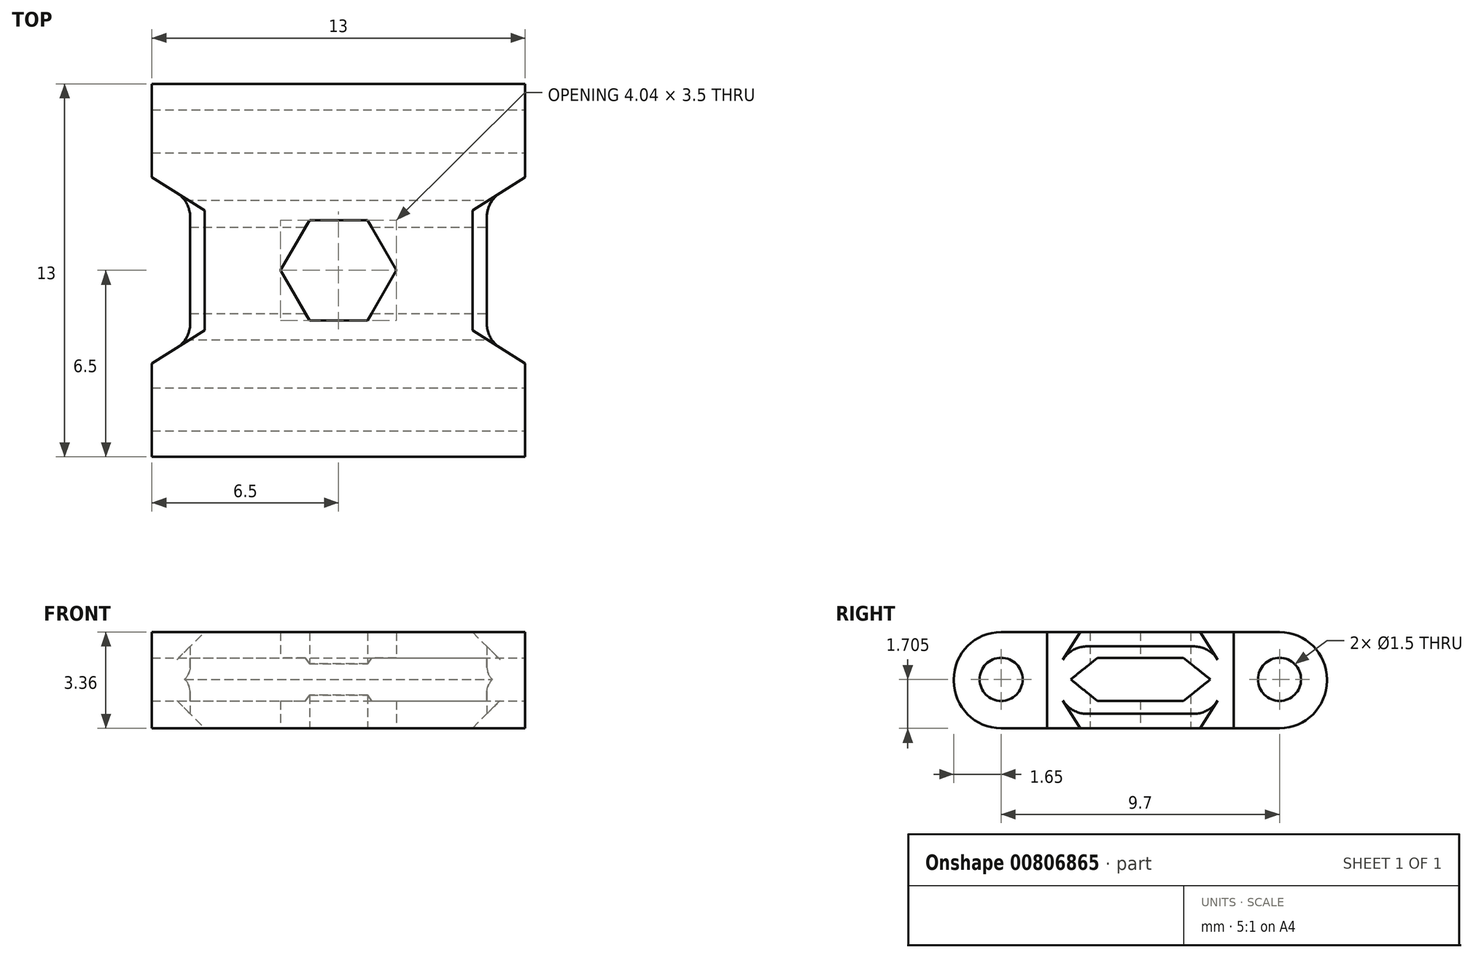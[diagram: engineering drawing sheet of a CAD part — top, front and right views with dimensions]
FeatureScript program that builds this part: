
annotation { "Feature Type Name" : "Feature", "Feature Type Description" : "" }
export const myFeature = defineFeature(function(context is Context, id is Id, definition is map)
    precondition{}
    {
        {
            var Q0;
            Q0=qCreatedBy(makeId("Top.planeOp"),FACE);
            var sketch = newSketch(context, id + "F0", { "sketchPlane" : qUnion([Q0])});
            skLineSegment(sketch, "E0.bottom", {"start": v(-6.5, 6.5) * mm, "end": v(6.5, 6.5) * mm});
            skLineSegment(sketch, "E0.top", {"start": v(-6.5, -6.5) * mm, "end": v(6.5, -6.5) * mm});
            skLineSegment(sketch, "E0.left", {"start": v(-6.5, 6.5) * mm, "end": v(-6.5, -6.5) * mm});
            skLineSegment(sketch, "E0.right", {"start": v(6.5, 6.5) * mm, "end": v(6.5, -6.5) * mm});
            skPoint(sketch, "E0.middle", {"position": v(0, 0) * mm});
            skLineSegment(sketch, "E1.bottom", {"start": v(-6.5, 3.25) * mm, "end": v(6.5, 3.25) * mm, "construction": true});
            skLineSegment(sketch, "E1.top", {"start": v(-6.5, -3.25) * mm, "end": v(6.5, -3.25) * mm, "construction": true});
            skLineSegment(sketch, "E1.left", {"start": v(-6.5, 3.25) * mm, "end": v(-6.5, -3.25) * mm, "construction": true});
            skLineSegment(sketch, "E1.right", {"start": v(6.5, 3.25) * mm, "end": v(6.5, -3.25) * mm, "construction": true});
            skLineSegment(sketch, "E2", {"start": v(-6.5, 3.25) * mm, "end": v(-5.17, 2.4) * mm});
            skLineSegment(sketch, "E3", {"start": v(-5.17, 2.4) * mm, "end": v(-5.17, -2.4) * mm});
            skLineSegment(sketch, "E4", {"start": v(-5.17, -2.4) * mm, "end": v(-6.5, -3.25) * mm});
            skLineSegment(sketch, "E5.MirrorCS", {"start": v(5.17, -2.4) * mm, "end": v(6.5, -3.25) * mm});
            skLineSegment(sketch, "E6.MirrorCS", {"start": v(6.5, 3.25) * mm, "end": v(5.17, 2.4) * mm});
            skLineSegment(sketch, "E7.MirrorCS", {"start": v(5.17, 2.4) * mm, "end": v(5.17, -2.4) * mm});
            skCircle(sketch, "E8.cCircle", {"center": v(0, 0) * mm, "radius": 1.75 * mm, "construction": true});
            skLineSegment(sketch, "E8.0", {"start": v(-1.01, 1.75) * mm, "end": v(1.01, 1.75) * mm});
            skLineSegment(sketch, "E8.1", {"start": v(1.01, 1.75) * mm, "end": v(2.02, 0) * mm});
            skLineSegment(sketch, "E8.2", {"start": v(2.02, 0) * mm, "end": v(1.01, -1.75) * mm});
            skLineSegment(sketch, "E8.3", {"start": v(1.01, -1.75) * mm, "end": v(-1.01, -1.75) * mm});
            skLineSegment(sketch, "E8.4", {"start": v(-1.01, -1.75) * mm, "end": v(-2.02, 0) * mm});
            skLineSegment(sketch, "E8.5", {"start": v(-2.02, 0) * mm, "end": v(-1.01, 1.75) * mm});
            skPoint(sketch, "E8.0.midPoint", {"position": v(0, 1.75) * mm});
            skSolve(sketch);
        }
        {
            var Q0;
            Q0=makeQuery(id+"F0.imprint","IMPRINT",FACE,{"disambiguationData":[TD([[makeQuery(id+"F0.imprint","IMPRINT",EDGE,{"derivedFrom":sQuery(id+"F0.wireOp",EDGE,"E0.bottom")}),-1.0]])]});
            extrude(context, id + "F1", {"entities" : qUnion([Q0]), "endBound" : BoundingType.SYMMETRIC, "depth" : 3.35 * mm, "offsetDistance" : 25.4 * mm});
        }
        {
            var Q0;
            Q0=makeQuery(id+"F1.opExtrude","CAP_EDGE",EDGE,{"disambiguationData":[OSD([sQuery(id+"F0.wireOp",EDGE,"E3")])],"isStart":false});
            var Q1;
            Q1=makeQuery(id+"F1.opExtrude","CAP_EDGE",EDGE,{"disambiguationData":[OSD([sQuery(id+"F0.wireOp",EDGE,"E7.MirrorCS")])],"isStart":false});
            var Q2;
            Q2=makeQuery(id+"F1.opExtrude","CAP_EDGE",EDGE,{"disambiguationData":[OSD([sQuery(id+"F0.wireOp",EDGE,"E3")])],"isStart":true});
            var Q3;
            Q3=makeQuery(id+"F1.opExtrude","CAP_EDGE",EDGE,{"disambiguationData":[OSD([sQuery(id+"F0.wireOp",EDGE,"E7.MirrorCS")])],"isStart":true});
            chamfer(context, id + "F2", {"entities" : qUnion([Q0, Q1, Q2, Q3]), "width" : .5 * mm, "tangentPropagation" : true});
        }
        {
            var Q0;
            Q0=makeQuery(id+"F1.opExtrude","CAP_EDGE",EDGE,{"disambiguationData":[OSD([sQuery(id+"F0.wireOp",EDGE,"E0.bottom")])],"isStart":false});
            var Q1;
            Q1=makeQuery(id+"F1.opExtrude","CAP_EDGE",EDGE,{"disambiguationData":[OSD([sQuery(id+"F0.wireOp",EDGE,"E0.bottom")])],"isStart":true});
            var Q2;
            Q2=makeQuery(id+"F1.opExtrude","CAP_EDGE",EDGE,{"disambiguationData":[OSD([sQuery(id+"F0.wireOp",EDGE,"E0.top")])],"isStart":false});
            var Q3;
            Q3=makeQuery(id+"F1.opExtrude","CAP_EDGE",EDGE,{"disambiguationData":[OSD([sQuery(id+"F0.wireOp",EDGE,"E0.top")])],"isStart":true});
            fillet(context, id + "F3", {"entities" : qUnion([Q0, Q1, Q2, Q3]), "radius" : 1.65 * mm, "tangentPropagation" : true, "allowEdgeOverflow" : false});
        }
        {
            var Q0;
            Q0=makeQuery(id+"F1.opExtrude","SWEPT_EDGE",EDGE,{"disambiguationData":[OSD([sQuery(id+"F0.wireOp",EDGE,"E6.MirrorCS"),sQuery(id+"F0.wireOp",EDGE,"E7.MirrorCS")])]});
            var Q1;
            Q1=makeQuery(id+"F1.opExtrude","SWEPT_EDGE",EDGE,{"disambiguationData":[OSD([sQuery(id+"F0.wireOp",EDGE,"E5.MirrorCS"),sQuery(id+"F0.wireOp",EDGE,"E7.MirrorCS")])]});
            var Q2;
            Q2=makeQuery(id+"F1.opExtrude","SWEPT_EDGE",EDGE,{"disambiguationData":[OSD([sQuery(id+"F0.wireOp",EDGE,"E3"),sQuery(id+"F0.wireOp",EDGE,"E4")])]});
            var Q3;
            Q3=makeQuery(id+"F1.opExtrude","SWEPT_EDGE",EDGE,{"disambiguationData":[OSD([sQuery(id+"F0.wireOp",EDGE,"E2"),sQuery(id+"F0.wireOp",EDGE,"E3")])]});
            fillet(context, id + "F4", {"entities" : qUnion([Q0, Q1, Q2, Q3]), "radius" : 1 * mm, "tangentPropagation" : true, "allowEdgeOverflow" : false});
        }
        {
            var Q0;
            Q0=makeQuery(id+"F1.opExtrude","SWEPT_FACE",FACE,{"disambiguationData":[OSD([sQuery(id+"F0.wireOp",EDGE,"E0.right")])]});
            var sketch = newSketch(context, id + "F5", { "sketchPlane" : qUnion([Q0])});
            skCircle(sketch, "E9", {"center": v(-4.85, 0.03) * mm, "radius": 0.75 * mm});
            skCircle(sketch, "E10", {"center": v(4.85, 0.03) * mm, "radius": 0.75 * mm});
            skLineSegment(sketch, "E11", {"start": v(-2.42, 0.03) * mm, "end": v(-1.5, 0.77) * mm});
            skLineSegment(sketch, "E12", {"start": v(-1.5, 0.77) * mm, "end": v(1.5, 0.77) * mm});
            skLineSegment(sketch, "E13", {"start": v(1.5, 0.77) * mm, "end": v(2.44, 0.03) * mm});
            skLineSegment(sketch, "E14", {"start": v(2.44, 0.03) * mm, "end": v(1.5, -0.72) * mm});
            skLineSegment(sketch, "E15", {"start": v(1.5, -0.72) * mm, "end": v(-1.5, -0.72) * mm});
            skLineSegment(sketch, "E16", {"start": v(-1.5, -0.72) * mm, "end": v(-2.42, 0.03) * mm});
            skLineSegment(sketch, "E17", {"start": v(-4.85, 0.03) * mm, "end": v(4.85, 0.03) * mm, "construction": true});
            skLineSegment(sketch, "E18.bottom", {"start": v(-1.5, 0.77) * mm, "end": v(1.5, 0.77) * mm, "construction": true});
            skLineSegment(sketch, "E18.top", {"start": v(-1.5, -0.72) * mm, "end": v(1.5, -0.72) * mm, "construction": true});
            skLineSegment(sketch, "E18.left", {"start": v(-1.5, 0.77) * mm, "end": v(-1.5, -0.72) * mm, "construction": true});
            skLineSegment(sketch, "E18.right", {"start": v(1.5, 0.77) * mm, "end": v(1.5, -0.72) * mm, "construction": true});
            skPoint(sketch, "E18.middle", {"position": v(0, 0.03) * mm});
            skSolve(sketch);
        }
        {
            var Q0;
            Q0=makeQuery(id+"F5.imprint","IMPRINT",FACE,{"disambiguationData":[TD([[makeQuery(id+"F5.imprint","IMPRINT",EDGE,{"derivedFrom":sQuery(id+"F5.wireOp",EDGE,"E9")}),1.0]])]});
            var Q1;
            Q1=makeQuery(id+"F5.imprint","IMPRINT",FACE,{"disambiguationData":[TD([[makeQuery(id+"F5.imprint","IMPRINT",EDGE,{"derivedFrom":sQuery(id+"F5.wireOp",EDGE,"E10")}),1.0]])]});
            var Q2;
            Q2=makeQuery(id+"F5.imprint","IMPRINT",FACE,{"disambiguationData":[TD([[makeQuery(id+"F5.imprint","IMPRINT",EDGE,{"derivedFrom":sQuery(id+"F5.wireOp",EDGE,"E11")}),-1.0]])]});
            extrude(context, id + "F6", {"entities" : qUnion([Q0, Q1, Q2]), "operationType" : NewBodyOperationType.REMOVE, "endBound" : BoundingType.THROUGH_ALL, "oppositeDirection" : true, "depth" : 25 * mm, "offsetDistance" : 25 * mm});
        }
    });
